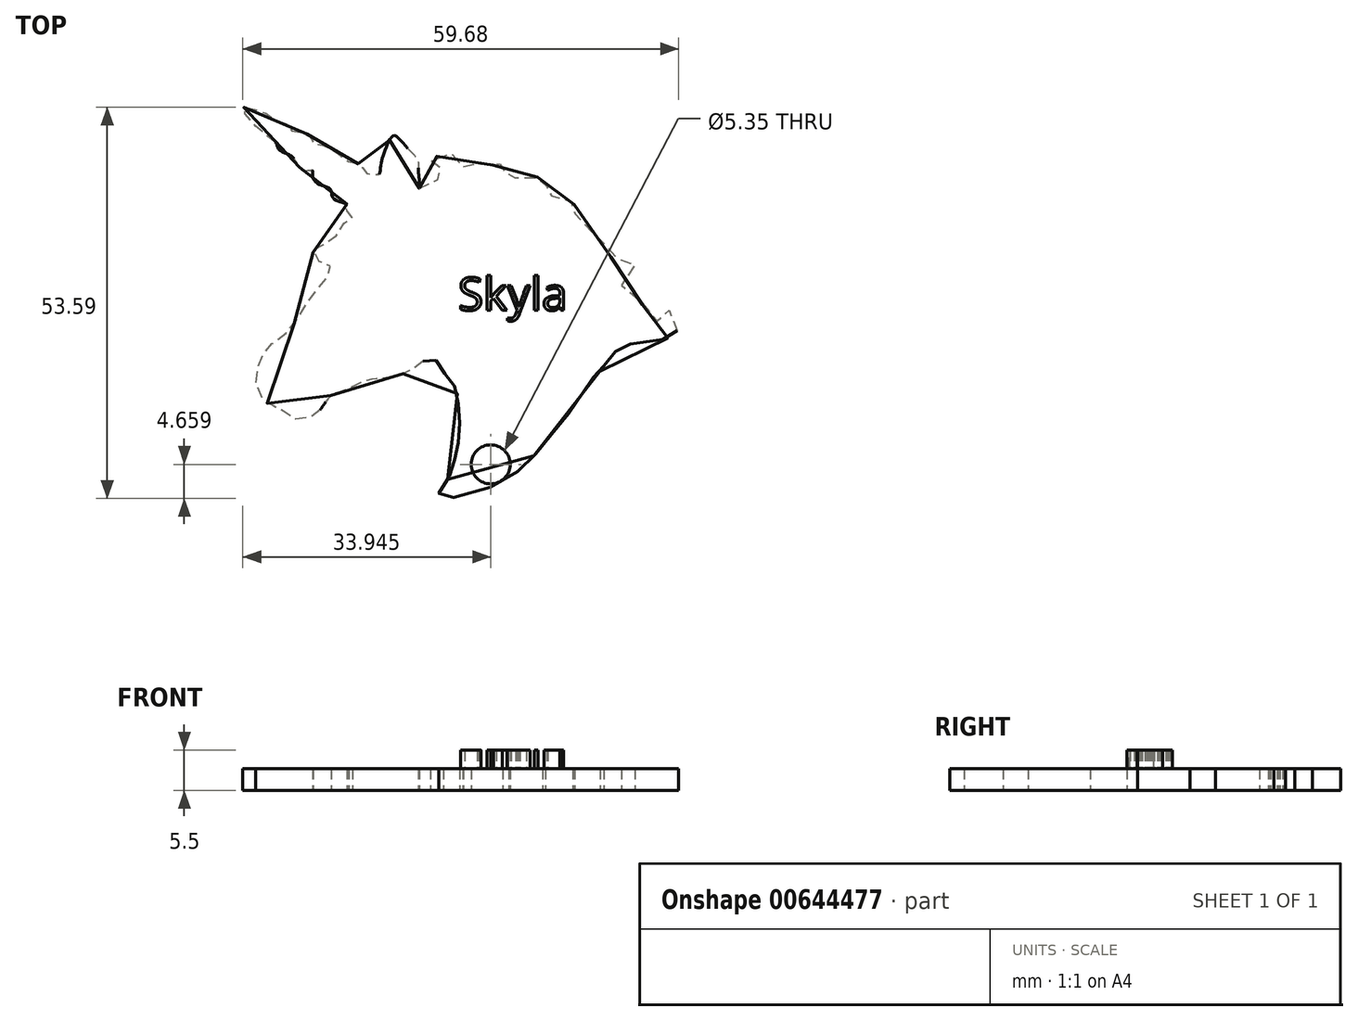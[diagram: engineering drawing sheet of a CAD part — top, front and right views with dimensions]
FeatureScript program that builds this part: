
annotation { "Feature Type Name" : "Feature", "Feature Type Description" : "" }
export const myFeature = defineFeature(function(context is Context, id is Id, definition is map)
    precondition{}
    {
        {
            var Q0;
            Q0=qCreatedBy(makeId("Top.planeOp"),FACE);
            var sketch = newSketch(context, id + "F0", { "sketchPlane" : qUnion([Q0])});
            skFitSpline(sketch, "E0", {"points": [v(30.83, 50.6) * mm, v(32.44, 51.73) * mm, v(33.75, 51.92) * mm, v(34.13, 53.05) * mm, v(33.75, 53.43) * mm, v(32.72, 53.24) * mm, v(32.44, 54.27) * mm, v(33.75, 55.22) * mm, v(35.73, 55.31) * mm, v(36.86, 54.27) * mm, v(36.86, 53.33) * mm, v(37.71, 53.9) * mm, v(39.5, 53.9) * mm, v(41.67, 53.9) * mm, v(43.08, 54.09) * mm, v(42.61, 52.67) * mm, v(42.33, 52.1) * mm, v(43.84, 52.1) * mm, v(45.54, 52.01) * mm, v(47.33, 52.3) * mm, v(47.8, 52.58) * mm, v(48.08, 50.5) * mm, v(47.8, 49.75) * mm, v(49.87, 49.47) * mm, v(50.9, 48.9) * mm, v(52.13, 48.71) * mm, v(51.85, 47.58) * mm, v(53.17, 46.45) * mm, v(54.68, 44.57) * mm, v(56.09, 44.47) * mm, v(55.62, 42.5) * mm, v(58.26, 40.99) * mm, v(59.86, 40.99) * mm, v(60.24, 39.2) * mm, v(58.54, 37.4) * mm, v(60.24, 36.18) * mm, v(62.03, 33.73) * mm, v(63.72, 32.41) * mm, v(64.95, 33.26) * mm, v(65.14, 33.92) * mm, v(66.36, 32.03) * mm, v(65.14, 30.24) * mm, v(63.06, 29.77) * mm, v(61, 29.49) * mm, v(58.92, 29.02) * mm, v(57.13, 27.7) * mm, v(55.62, 25.63) * mm, v(54.3, 24.3) * mm, v(52.5, 21.38) * mm, v(49.12, 17.14) * mm, v(46, 13.37) * mm, v(40.63, 9.7) * mm, v(33.57, 8.38) * mm, v(34.5, 10.36) * mm, v(35.55, 12.8) * mm, v(36.02, 14.88) * mm, v(36.4, 17.9) * mm, v(36.2, 20.72) * mm, v(35.83, 23.27) * mm, v(34.6, 24.87) * mm, v(33.57, 26.57) * mm, v(32.34, 27.42) * mm, v(30.55, 26.28) * mm, v(28.1, 25.06) * mm, v(25.93, 24.59) * mm, v(23.67, 24.3) * mm, v(21.4, 23.27) * mm, v(19.9, 22.7) * mm, v(18.77, 22.23) * mm, v(17.73, 20.91) * mm, v(16.41, 19.5) * mm, v(13.78, 19.03) * mm, v(11.8, 20.44) * mm, v(10.29, 21) * mm, v(8.5, 23.83) * mm, v(9.16, 27.23) * mm, v(10.1, 28.83) * mm, v(13.02, 31.19) * mm, v(15.19, 34.48) * mm, v(17.36, 37.31) * mm, v(18.77, 39.86) * mm, v(17.26, 40.52) * mm, v(16.41, 42.4) * mm, v(18.87, 43.34) * mm, v(20.37, 45.7) * mm, v(21.7, 46.55) * mm, v(20.94, 47.3) * mm, v(21.22, 48.24) * mm, v(19.15, 49.19) * mm, v(18.68, 50.5) * mm, v(17.17, 51.16) * mm, v(16.23, 52.3) * mm, v(16.23, 53.05) * mm, v(14.9, 53.05) * mm, v(13.59, 54.84) * mm, v(11.7, 55.88) * mm, v(11.23, 56.82) * mm, v(9.25, 58.42) * mm, v(6.7, 61.63) * mm, v(8.6, 61.34) * mm, v(10.38, 60.59) * mm, v(10.95, 60.02) * mm, v(12.93, 59.27) * mm, v(13.5, 58.42) * mm, v(15.57, 58.04) * mm, v(16.32, 56.82) * mm, v(17.73, 56.54) * mm, v(18.96, 55.88) * mm, v(20.28, 54.93) * mm, v(20.75, 54.46) * mm, v(21.88, 54.18) * mm, v(22.92, 53.61) * mm, v(23.67, 52.67) * mm, v(24.7, 52.48) * mm, v(25.27, 52.48) * mm, v(25.56, 53.52) * mm, v(25.84, 54.93) * mm, v(26.69, 57) * mm, v(27.44, 57.86) * mm, v(28.95, 56.44) * mm, v(30.65, 54.46) * mm, v(30.74, 53.05) * mm, v(30.83, 51.54) * mm, v(30.83, 50.6) * mm]});
            skCircle(sketch, "E1", {"center": v(40.63, 12.8) * mm, "radius": 2.67 * mm});
            skSolve(sketch);
        }
        {
            var Q0;
            Q0=makeQuery(id+"F0.imprint","IMPRINT",FACE,{"disambiguationData":[TD([[makeQuery(id+"F0.imprint","IMPRINT",EDGE,{"derivedFrom":sQuery(id+"F0.wireOp",EDGE,"E0")}),-1.0]])]});
            extrude(context, id + "F1", {"entities" : qUnion([Q0]), "depth" : 3 * mm, "offsetDistance" : 25.4 * mm});
        }
        {
            var Q0;
            Q0=makeQuery(id+"F1.opExtrude","CAP_FACE",FACE,{"disambiguationData":[OSD([sQuery(id+"F0.wireOp",EDGE,"E0"),sQuery(id+"F0.wireOp",EDGE,"E1")])],"isStart":false});
            var sketch = newSketch(context, id + "F2", { "sketchPlane" : qUnion([Q0])});
            skText(sketch, "E2", { "text": "Skyla", "fontName": "OpenSans-Regular.ttf"});
            const initialGuessF2  = {"E2": [0.03617, 0.03392, 1, 0, 0.00451]};
            skSetInitialGuess(sketch, initialGuessF2);
            skSolve(sketch);
        }
        {
            var Q0;
            Q0 = qSketchRegion(id + "F2", true);
            extrude(context, id + "F3", {"entities" : qUnion([Q0]), "operationType" : NewBodyOperationType.ADD, "depth" : 2.5 * mm, "offsetDistance" : 25 * mm});
        }
    });
